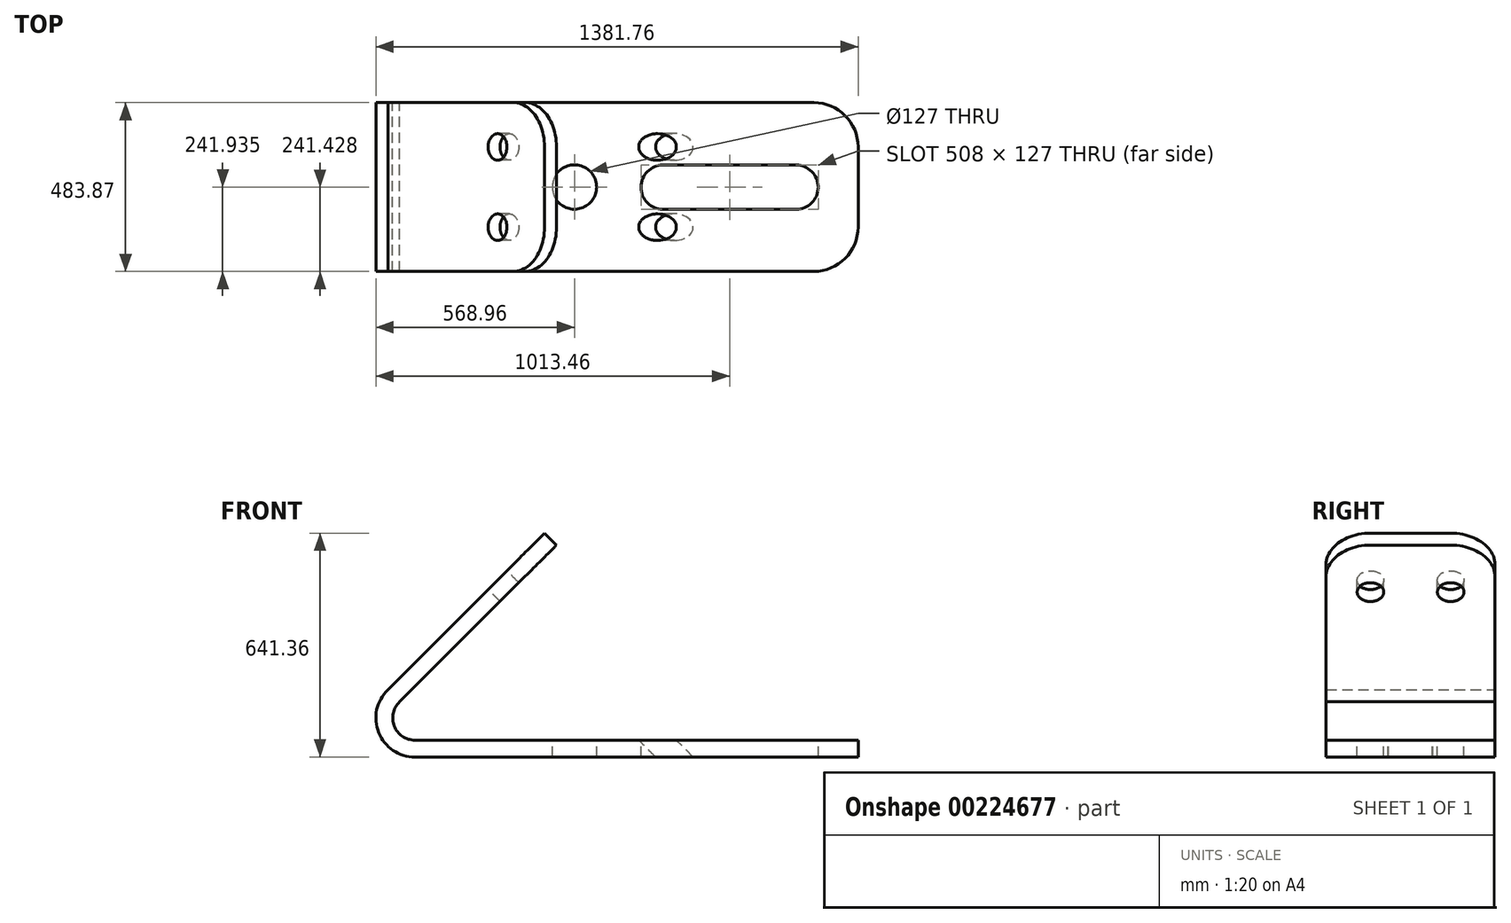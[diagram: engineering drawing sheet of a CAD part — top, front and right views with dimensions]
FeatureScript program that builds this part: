
annotation { "Feature Type Name" : "Feature", "Feature Type Description" : "" }
export const myFeature = defineFeature(function(context is Context, id is Id, definition is map)
    precondition{}
    {
        {
            var Q0;
            Q0=qCreatedBy(makeId("Front.planeOp"),FACE);
            var sketch = newSketch(context, id + "F0", { "sketchPlane" : qUnion([Q0])});
            skLineSegment(sketch, "E0.bottom", {"start": v(0, 0) * mm, "end": v(1270, 0) * mm});
            skLineSegment(sketch, "E0.top", {"start": v(0, -48.26) * mm, "end": v(1270, -48.26) * mm});
            skLineSegment(sketch, "E0.left", {"start": v(0, 0) * mm, "end": v(0, -48.26) * mm});
            skLineSegment(sketch, "E0.right", {"start": v(1270, 0) * mm, "end": v(1270, -48.26) * mm});
            skArc(sketch, "E1", {"start": v(-77.43, 144.09) * mm, "mid": v(-103.67, 21.76) * mm, "end": v(0, -48.26) * mm});
            skLineSegment(sketch, "E2", {"start": v(-77.43, 144.09) * mm, "end": v(371.58, 593.1) * mm});
            skLineSegment(sketch, "E3", {"start": v(371.58, 593.1) * mm, "end": v(405.7, 558.98) * mm});
            skLineSegment(sketch, "E4", {"start": v(405.7, 558.98) * mm, "end": v(-43.3, 109.96) * mm});
            skArc(sketch, "E5", {"start": v(-43.3, 109.96) * mm, "mid": v(-59.1, 40.24) * mm, "end": v(0, 0) * mm});
            skSolve(sketch);
        }
        {
            var Q0;
            Q0 = qSketchRegion(id + "F0", true);
            extrude(context, id + "F1", {"entities" : qUnion([Q0]), "depth" : 483.87 * mm});
        }
        {
            var Q0;
            Q0=makeQuery(id+"F1.opExtrude","SWEPT_FACE",FACE,{"disambiguationData":[OSD([sQuery(id+"F0.wireOp",EDGE,"E0.bottom")])]});
            var sketch = newSketch(context, id + "F2", { "sketchPlane" : qUnion([Q0])});
            skPoint(sketch, "E6.endSnap0", {"position": v(1270, -241.94) * mm});
            skCircle(sketch, "E7", {"center": v(457.2, -241.94) * mm, "radius": 63.5 * mm});
            skLineSegment(sketch, "E8", {"start": v(1092.2, -178.94) * mm, "end": v(711.2, -178.94) * mm});
            skLineSegment(sketch, "E9", {"start": v(711.2, -305.94) * mm, "end": v(1092.2, -305.94) * mm});
            skArc(sketch, "E10", {"start": v(711.2, -178.94) * mm, "mid": v(647.7, -242.44) * mm, "end": v(711.2, -305.94) * mm});
            skArc(sketch, "E11", {"start": v(1092.2, -305.94) * mm, "mid": v(1155.7, -242.44) * mm, "end": v(1092.2, -178.94) * mm});
            skSolve(sketch);
        }
        {
            var Q0;
            Q0=makeQuery(id+"F2.imprint","IMPRINT",FACE,{"disambiguationData":[TD([[makeQuery(id+"F2.imprint","IMPRINT",EDGE,{"derivedFrom":sQuery(id+"F2.wireOp",EDGE,"E7")}),1.0]])]});
            var Q1;
            Q1=makeQuery(id+"F2.imprint","IMPRINT",FACE,{"disambiguationData":[TD([[makeQuery(id+"F2.imprint","IMPRINT",EDGE,{"derivedFrom":sQuery(id+"F2.wireOp",EDGE,"E8")}),1.0]])]});
            extrude(context, id + "F3", {"entities" : qUnion([Q0, Q1]), "operationType" : NewBodyOperationType.REMOVE, "endBound" : BoundingType.THROUGH_ALL, "oppositeDirection" : true, "depth" : 25.4 * mm});
        }
        {
            var Q0;
            Q0=makeQuery(id+"F1.opExtrude","CAP_EDGE",EDGE,{"disambiguationData":[OSD([sQuery(id+"F0.wireOp",EDGE,"E3")])],"isStart":true});
            var Q1;
            Q1=makeQuery(id+"F1.opExtrude","CAP_EDGE",EDGE,{"disambiguationData":[OSD([sQuery(id+"F0.wireOp",EDGE,"E3")])],"isStart":false});
            var Q2;
            Q2=makeQuery(id+"F1.opExtrude","CAP_EDGE",EDGE,{"disambiguationData":[OSD([sQuery(id+"F0.wireOp",EDGE,"E0.right")])],"isStart":false});
            var Q3;
            Q3=makeQuery(id+"F1.opExtrude","CAP_EDGE",EDGE,{"disambiguationData":[OSD([sQuery(id+"F0.wireOp",EDGE,"E0.right")])],"isStart":true});
            fillet(context, id + "F4", {"entities" : qUnion([Q0, Q1, Q2, Q3]), "radius" : 127 * mm, "tangentPropagation" : true, "allowEdgeOverflow" : false});
        }
        {
            var Q0;
            Q0=makeQuery(id+"F1.opExtrude","SWEPT_FACE",FACE,{"disambiguationData":[OSD([sQuery(id+"F0.wireOp",EDGE,"E2")])]});
            var sketch = newSketch(context, id + "F5", { "sketchPlane" : qUnion([Q0])});
            skLineSegment(sketch, "E12", {"start": v(356.87, 682.13) * mm, "end": v(356.87, 491.63) * mm, "construction": true});
            skLineSegment(sketch, "E13", {"start": v(127, 682.13) * mm, "end": v(127, 491.63) * mm, "construction": true});
            skCircle(sketch, "E14", {"center": v(127, 491.63) * mm, "radius": 38.1 * mm});
            skCircle(sketch, "E15", {"center": v(356.87, 491.63) * mm, "radius": 38.1 * mm});
            skSolve(sketch);
        }
        {
            var Q0;
            Q0=makeQuery(id+"F5.imprint","IMPRINT",FACE,{"disambiguationData":[TD([[makeQuery(id+"F5.imprint","IMPRINT",EDGE,{"derivedFrom":sQuery(id+"F5.wireOp",EDGE,"E14")}),1.0]])]});
            var Q1;
            Q1=makeQuery(id+"F5.imprint","IMPRINT",FACE,{"disambiguationData":[TD([[makeQuery(id+"F5.imprint","IMPRINT",EDGE,{"derivedFrom":sQuery(id+"F5.wireOp",EDGE,"E15")}),1.0]])]});
            extrude(context, id + "F6", {"entities" : qUnion([Q0, Q1]), "operationType" : NewBodyOperationType.REMOVE, "endBound" : BoundingType.THROUGH_ALL, "oppositeDirection" : true, "depth" : 25.4 * mm});
        }
    });
